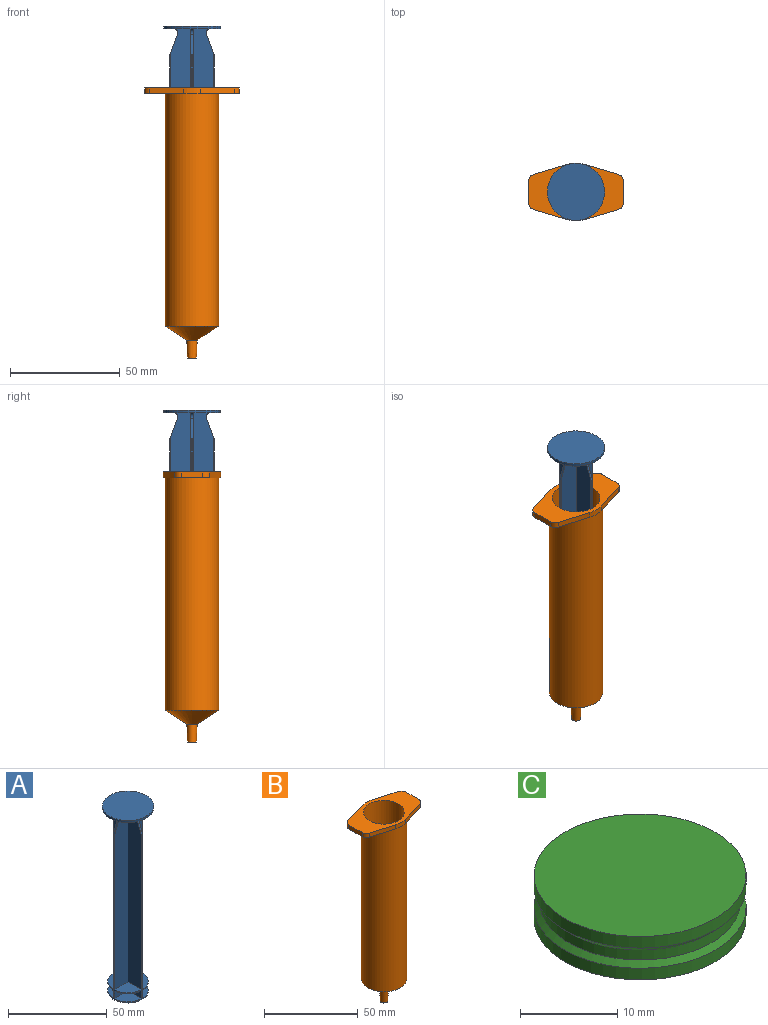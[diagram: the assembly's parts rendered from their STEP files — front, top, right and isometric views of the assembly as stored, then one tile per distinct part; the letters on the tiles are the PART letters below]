
ASSEMBLY  parts=3 mates=3
PART A: 57 faces, bbox 26x26x115.1 mm
  f0: plane 9.42x4.8mm, normal (0,-1,0), area 45.2mm2, adj f1,f19,f20,f24
  f1: plane 9.42x4.8mm, normal (-1,0,0), area 45.2mm2, adj f0,f2,f20,f24
  f2: cylinder r=0.2mm len=4.8mm, axis (0,0,-1), area 1.5mm2, adj f1,f3,f20,f24
  f3: plane 4.8x0.57mm, normal (0,-1,0), area 2.7mm2, adj f2,f4,f20,f24
  f4: cylinder r=0.2mm len=4.8mm, axis (0,0,-1), area 1.5mm2, adj f3,f5,f20,f24
  f5: plane 9.42x4.8mm, normal (1,0,0), area 45.2mm2, adj f4,f6,f20,f24
  f6: plane 9.42x4.8mm, normal (0,-1,0), area 45.2mm2, adj f5,f7,f20,f24
  f7: cylinder r=0.2mm len=4.8mm, axis (0,0,-1), area 1.5mm2, adj f6,f8,f20,f24
  f8: plane 4.8x0.57mm, normal (1,0,0), area 2.7mm2, adj f7,f9,f20,f24
  f9: cylinder r=0.2mm len=4.8mm, axis (0,0,-1), area 1.5mm2, adj f8,f10,f20,f24
  f10: plane 9.42x4.8mm, normal (0,1,0), area 45.2mm2, adj f9,f11,f20,f24
  f11: plane 9.42x4.8mm, normal (1,0,0), area 45.2mm2, adj f10,f12,f20,f24
  f12: cylinder r=0.2mm len=4.8mm, axis (0,0,-1), area 1.5mm2, adj f11,f13,f20,f24
  f13: plane 4.8x0.57mm, normal (0,1,0), area 2.7mm2, adj f12,f14,f20,f24
  f14: cylinder r=0.2mm len=4.8mm, axis (0,0,-1), area 1.5mm2, adj f13,f15,f20,f24
  f15: plane 9.42x4.8mm, normal (-1,0,0), area 45.2mm2, adj f14,f16,f20,f24
  f16: plane 9.42x4.8mm, normal (0,1,0), area 45.2mm2, adj f15,f17,f20,f24
  f17: cylinder r=0.2mm len=4.8mm, axis (0,0,-1), area 1.5mm2, adj f16,f18,f20,f24
  f18: plane 4.8x0.57mm, normal (-1,0,0), area 2.7mm2, adj f17,f19,f20,f24
  f19: cylinder r=0.2mm len=4.8mm, axis (0,0,-1), area 1.5mm2, adj f0,f18,f20,f24
  f20: plane 20.5x20.5mm, normal (0,0,1), area 291.5mm2, adj f0,f1,f2,f3,f4,f5,f6,f7
  f21: cylinder r=10.25mm len=20.5mm, axis (0,0,-1), area 50.7mm2, adj f20,f22
  f22: plane 20.5x20.5mm, normal (0,0,-1), area 330mm2, adj f21
  f23: plane 20.5x20.5mm, normal (0,0,1), area 291.5mm2, adj f25,f26,f27,f28,f29,f30,f31,f32
  f24: plane 20.5x20.5mm, normal (0,0,-1), area 291.5mm2, adj f0,f1,f2,f3,f4,f5,f6,f7
  f25: cylinder r=10.25mm len=20.5mm, axis (0,0,-1), area 49.1mm2, adj f23,f24
  f26: cylinder r=0.2mm len=96.09mm, axis (0,0,-1), area 30.6mm2, adj f23,f27,f45,f50
  f27: plane 95.6x0.6mm, normal (-1,0,0), area 54.6mm2, adj f23,f26,f28,f50
  f28: cylinder r=0.2mm len=96.09mm, axis (0,0,-1), area 30.6mm2, adj f23,f27,f29,f50
  f29: plane 107.51x9.46mm, normal (0,1,0), area 989.6mm2, adj f23,f28,f30,f46,f49,f50
  f30: plane 107.51x9.46mm, normal (-1,0,0), area 989.6mm2, adj f23,f29,f31,f46,f55,f56
  f31: cylinder r=0.2mm len=96.09mm, axis (0,0,-1), area 30.6mm2, adj f23,f30,f32,f55
  f32: plane 95.6x0.6mm, normal (0,1,0), area 54.6mm2, adj f23,f31,f33,f55
  f33: cylinder r=0.2mm len=96.09mm, axis (0,0,-1), area 30.6mm2, adj f23,f32,f34,f55
  f34: plane 107.51x9.46mm, normal (1,0,0), area 989.6mm2, adj f23,f33,f35,f46,f55,f56
  f35: plane 107.51x9.46mm, normal (0,1,0), area 989.6mm2, adj f23,f34,f36,f46,f53,f54
  f36: cylinder r=0.2mm len=96.09mm, axis (0,0,-1), area 30.6mm2, adj f23,f35,f37,f54
  f37: plane 95.6x0.6mm, normal (1,0,0), area 54.6mm2, adj f23,f36,f38,f54
  f38: cylinder r=0.2mm len=96.09mm, axis (0,0,-1), area 30.6mm2, adj f23,f37,f39,f54
  f39: plane 107.51x9.46mm, normal (0,-1,0), area 989.6mm2, adj f23,f38,f40,f46,f53,f54
  f40: plane 107.51x9.46mm, normal (1,0,0), area 989.6mm2, adj f23,f39,f41,f46,f51,f52
  f41: cylinder r=0.2mm len=96.09mm, axis (0,0,-1), area 30.6mm2, adj f23,f40,f42,f52
  f42: plane 95.6x0.6mm, normal (0,-1,0), area 54.6mm2, adj f23,f41,f43,f52
  f43: cylinder r=0.2mm len=96.09mm, axis (0,0,-1), area 30.6mm2, adj f23,f42,f44,f52
  f44: plane 107.51x9.46mm, normal (-1,0,0), area 989.6mm2, adj f23,f43,f45,f46,f51,f52
  f45: plane 107.51x9.46mm, normal (0,-1,0), area 989.6mm2, adj f23,f26,f44,f46,f49,f50
  f46: plane 25.98x25.98mm, normal (0,0,-1), area 498.8mm2, adj f29,f30,f34,f35,f39,f40,f44,f45
  f47: cylinder r=12.99mm len=25.98mm, axis (0,0,-1), area 103.7mm2, adj f46,f48
  f48: plane 25.98x25.98mm, normal (0,0,1), area 530.3mm2, adj f47
  f49: torus R=8.31mm, axis (0,0,1), area 3.4mm2, adj f29,f45,f46,f50
  f50: cone r=10.23mm half-angle=20.3deg, axis (0,0,-1), area 10mm2, adj f26,f27,f28,f29,f45,f49
  f51: torus R=8.31mm, axis (0,0,1), area 3.4mm2, adj f40,f44,f46,f52
  f52: cone r=10.23mm half-angle=20.3deg, axis (0,0,-1), area 10mm2, adj f40,f41,f42,f43,f44,f51
  f53: torus R=8.31mm, axis (0,0,1), area 3.4mm2, adj f35,f39,f46,f54
  f54: cone r=10.23mm half-angle=20.3deg, axis (0,0,-1), area 10mm2, adj f35,f36,f37,f38,f39,f53
  f55: cone r=10.23mm half-angle=20.3deg, axis (0,0,-1), area 10mm2, adj f30,f31,f32,f33,f34,f56
  f56: torus R=8.31mm, axis (0,0,1), area 3.4mm2, adj f30,f34,f46,f55
PART B: 21 faces, bbox 43x26.3x122.9 mm
  f0: plane 42.98x26.29mm, normal (0,0,1), area 522.8mm2, adj f6,f9,f10,f11,f12,f13,f14,f15
  f1: plane 42.98x26.29mm, normal (0,0,-1), area 436.4mm2, adj f7,f9,f10,f11,f12,f13,f14,f15
  f2: cone r=2.03mm half-angle=2.2deg, axis (0,0,1), area 112.8mm2, adj f3,f8
  f3: plane 4.06x4.06mm, normal (0,0,-1), area 10.2mm2, adj f2,f4
  f4: cone r=1.33mm half-angle=2.2deg, axis (0,0,1), area 70.8mm2, adj f3,f5
  f5: cone r=10.92mm half-angle=57.3deg, axis (0,0,1), area 438.7mm2, adj f4,f6
  f6: cylinder r=10.92mm len=106.84mm, axis (0,0,-1), area 7332mm2, adj f0,f5
  f7: cylinder r=12.12mm len=105.85mm, axis (0,0,-1), area 8058.3mm2, adj f1,f8
  f8: cone r=2.35mm half-angle=57.3deg, axis (0,0,1), area 527.3mm2, adj f2,f7
  f9: cylinder r=3.17mm len=3.04mm, axis (0,0,1), area 10.7mm2, adj f0,f1,f10,f18
  f10: plane 9.94x2.63mm, normal (-1,0,0), area 26.1mm2, adj f0,f1,f9,f11
  f11: cylinder r=3.17mm len=3.04mm, axis (0,0,1), area 10.7mm2, adj f0,f1,f10,f17
  f12: cylinder r=3.17mm len=3.04mm, axis (0,0,1), area 10.7mm2, adj f0,f1,f13,f15
  f13: plane 9.94x2.63mm, normal (1,0,0), area 26.1mm2, adj f0,f1,f12,f14
  f14: cylinder r=3.17mm len=3.04mm, axis (0,0,1), area 10.7mm2, adj f0,f1,f13,f20
  f15: plane 15.48x4.59mm, normal (0.28,-0.96,0), area 42.4mm2, adj f0,f1,f12,f16
  f16: cylinder r=13.14mm len=7.47mm, axis (0,0,1), area 19.9mm2, adj f0,f1,f15,f17
  f17: plane 15.48x4.59mm, normal (-0.28,-0.96,0), area 42.4mm2, adj f0,f1,f11,f16
  f18: plane 15.48x4.59mm, normal (-0.28,0.96,0), area 42.4mm2, adj f0,f1,f9,f19
  f19: cylinder r=13.14mm len=7.47mm, axis (0,0,1), area 19.9mm2, adj f0,f1,f18,f20
  f20: plane 15.48x4.59mm, normal (0.28,0.96,0), area 42.4mm2, adj f0,f1,f14,f19
PART C: 8 faces, bbox 21.8x21.8x11.6 mm
  f0: plane 21.84x21.84mm, normal (0,0,1), area 374.8mm2, adj f1
  f1: cylinder r=10.92mm len=21.84mm, axis (0,0,1), area 100.2mm2, adj f0,f2
  f2: cone r=10.92mm half-angle=42.3deg, axis (0,0,1), area 57.4mm2, adj f1,f3
  f3: cylinder r=10.34mm len=20.69mm, axis (0,0,1), area 82.5mm2, adj f2,f4
  f4: cone r=10.34mm half-angle=42.3deg, axis (0,0,-1), area 57.4mm2, adj f3,f5
  f5: cylinder r=10.92mm len=21.84mm, axis (0,0,1), area 100.2mm2, adj f4,f6
  f6: cone r=1.33mm half-angle=57.3deg, axis (0,0,1), area 438.7mm2, adj f5,f7
  f7: plane 2.65x2.65mm, normal (0,0,-1), area 5.5mm2, adj f6
PLACE A t=(104.26,16.66,-41.92)mm
PLACE B t=(104.26,16.66,-56.37)mm
PLACE C t=(104.26,16.66,-41.92)mm
MATE slider C.f1 <-> B.f2  axis (0,0,1) through (104.26,16.66,-100.36)mm
MATE cylindrical A.f21 <-> C.f1  axis (0,0,-1) through (104.26,16.66,-95.63)mm
MATE planar A.f21 <-> C.f1  axis (0,0,-1) through (104.26,16.66,-95.63)mm
